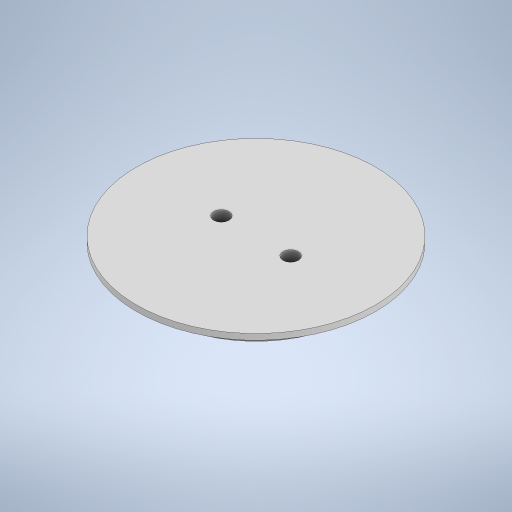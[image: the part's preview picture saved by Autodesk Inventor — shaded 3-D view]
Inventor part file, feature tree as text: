
AUTODESK INVENTOR PART (.ipt)
format: ipt  version: 2023 (Build 270158000, 158)  size: 245,248 bytes
history: native  units: in
note: dims shown in document units (in); Inventor stores cm internally (conversion verified against a paired STEP export)
features: extrude x3, sketch x3
ambient origin geometry x8: Origin, YZ Plane, XZ Plane, XY Plane, X Axis, Y Axis, Z Axis, Center Point
bodies: Solid1 (feature_tree)
feature tree (6):
  extrude  "Extrusion1"  Depth=0.3543in
  extrude  "Extrusion2"  Depth=0.3543in
  extrude  "Extrusion4"  Depth=0.1181in TaperAngle=0.0deg
  sketch  "Sketch1"  dims[d0=1.063in d1=0.3543in]
  sketch  "Sketch2"  dims[d2=0.3543in d3=0.1575in]
  sketch  "Sketch3"  dims[d4=0.1575in d5=0.1181in d6=0.0in d7=1.9685in d8=0.1772in d9=0.0in d10=2.4409in d13=0.0591in d14=0.0in]
